# Revit family: PRD_FrankeWS_SnksSuprts_MaximaUnderframeToCommercialSinks_MAXF
name_source: partatom
category: Plumbing Fixtures
revit_build: Autodesk Revit 2018 (Build: 20190510_1515(x64)
units: mm (PartAtom-declared; Revit-internal decimal feet)

## family parameters
Always vertical = Yes
Cut with Voids When Loaded = No
OmniClass Number = 23.40.20.00
OmniClass Title = General Furniture and Specialties
Part Type = Normal
Room Calculation Point = No
Round Connector Dimension = Use Diameter
Shared = Yes
Work Plane-Based = No

## types (12) — shared parameters
AssetType = Fixed
Category = Pr_20_85_09_88, Sink supports
Color = stainless steel
DurationUnit = year
Features = stainless steel, 1.00 mm, satin finished, no mounting
Finish = satin finished
Form = Floor-standing
Height = 850 mm  [stored 2.78871 ft]
IfcExportAs = IfcBuildingElementProxy
IfcExportType = NOTDEFINED
Manufacturer = KWC Group AG
ManufacturerName = KWC Group AG
ManufacturerURL = www.kwc.com
Material = stainless steel
MaterialCode = stainless steel 1.4301
MaterialThickness = 1 mm  [stored 0.00328084 ft]
MaterialsBracketsBody = stainless steel
MaterialsBracketsFinishAndColour = satin finished
MaterialsLegsBody = stainless steel
MaterialsLegsFinishAndColour = satin finished
NBSDescription = Supports for sinks
NBSReference = 45-35-70/347
NominalHeight = 850 mm  [stored 2.78871 ft]
ProductInformation = https://pim.kwc.com
Shape = Rectangular
URL = www.kwc.com
UnderframeMaterial = PRD_AR_StainlessSteel_SatinFinished
Uniclass2015Code = Pr_20_85_09_88
Uniclass2015Title = Sink supports
Uniclass2015Version = Products v1.10
Version = 1
WarrantyDurationUnit = year

## per-type parameters (varying)
| type | BIMObjectName | Description | GrossWeight | Length | MAXF260 | MAXF60-200 | ModelNumber | Name | NetWeight | NominalLength | NominalWidth | Size | Width |
| MAXF60-60 | PRD_AR_SinkSupports_MaximaUnderframeToCommercialSinks_MAXF60-60 | Underframe to Maxima, stainless steel, 1.00 mm, satin finished,580x850x550 mm (WxHxD) | 32.00 kg | 580 mm  [stored 1.90289 ft] | No | Yes | 2000057122 | Underframe to Maxima sinks width 600 mm / depth 600 mm | 12.00 kg | 580 mm  [stored 1.90289 ft] | 550 mm | 580 x 550 x 850 mm | 550 mm |
| MAXF70-60 | PRD_AR_SinkSupports_MaximaUnderframeToCommercialSinks_MAXF70-60 | Underframe to Maxima, stainless steel, 1.00 mm, satin finished,680x850x550 mm (WxHxD) | 32.50 kg | 680 mm  [stored 2.23097 ft] | No | Yes | 2000057124 | Underframe to Maxima sinks width 700 mm / depth 600 mm | 12.50 kg | 680 mm  [stored 2.23097 ft] | 550 mm | 680 x 550 x 850 mm | 550 mm |
| MAXF70-70 | PRD_AR_SinkSupports_MaximaUnderframeToCommercialSinks_MAXF70-70 | Underframe to Maxima, stainless steel, 1.00 mm, satin finished,680x850x650 mm (WxHxD) | 33.50 kg | 680 mm  [stored 2.23097 ft] | No | Yes | 2000057126 | Underframe to Maxima sinks width 700 mm / depth 700 mm | 13.50 kg | 680 mm  [stored 2.23097 ft] | 650 mm  [stored 2.13255 ft] | 680 x 650 x 850 mm | 650 mm  [stored 2.13255 ft] |
| MAXF120-60 | PRD_AR_SinkSupports_MaximaUnderframeToCommercialSinks_MAXF120-60 | Underframe to Maxima, stainless steel, 1.00 mm, satin finished,1180x850x550 mm (WxHxD) | 35.00 kg | 1180 mm  [stored 3.87139 ft] | No | Yes | 2000057101 | Underframe to Maxima sinks width 1200 mm / depth 600 mm | 15.00 kg | 1180 mm  [stored 3.87139 ft] | 550 mm | 1180 x 550 x 850 mm | 550 mm |
| MAXF120-70 | PRD_AR_SinkSupports_MaximaUnderframeToCommercialSinks_MAXF120-70 | Underframe to Maxima, stainless steel, 1.00 mm, satin finished,1180x850x650 mm (WxHxD) | 36.00 kg | 1180 mm  [stored 3.87139 ft] | No | Yes | 2000057104 | Underframe to Maxima sinks width 1200 mm / depth 700 mm | 16.00 kg | 1180 mm  [stored 3.87139 ft] | 650 mm  [stored 2.13255 ft] | 1180 x 650 x 850 mm | 650 mm  [stored 2.13255 ft] |
| MAXF140-60 | PRD_AR_SinkSupports_MaximaUnderframeToCommercialSinks_MAXF140-60 | Underframe to Maxima, stainless steel, 1.00 mm, satin finished,1380x850x550 mm (WxHxD) | 33.50 kg | 1380 mm  [stored 4.52756 ft] | No | Yes | 2000057106 | Underframe to Maxima sinks width 1400 mm / depth 600 mm | 13.50 kg | 1380 mm  [stored 4.52756 ft] | 550 mm | 1380 x 550 x 850 mm | 550 mm |
| MAXF140-70 | PRD_AR_SinkSupports_MaximaUnderframeToCommercialSinks_MAXF140-70 | Underframe to Maxima, stainless steel, 1.00 mm, satin finished,1380x850x650 mm (WxHxD) | 36.50 kg | 1380 mm  [stored 4.52756 ft] | No | Yes | 2000057108 | Underframe to Maxima sinks width 1400 mm / depth 700 mm | 16.50 kg | 1380 mm  [stored 4.52756 ft] | 650 mm  [stored 2.13255 ft] | 1380 x 650 x 850 mm | 650 mm  [stored 2.13255 ft] |
| MAXF160-60 | PRD_AR_SinkSupports_MaximaUnderframeToCommercialSinks_MAXF160-60 | Underframe to Maxima, stainless steel, 1.00 mm, satin finished,1580x850x550 mm (WxHxD) | 34.50 kg | 1580 mm  [stored 5.18373 ft] | No | Yes | 2000057112 | Underframe to Maxima sinks width 1600 mm / depth 600 mm | 14.50 kg | 1580 mm  [stored 5.18373 ft] | 550 mm | 1580 x 550 x 850 mm | 550 mm |
| MAXF200-60 | PRD_AR_SinkSupports_MaximaUnderframeToCommercialSinks_MAXF200-60 | Underframe to Maxima, stainless steel, 1.00 mm, satin finished,1980x850x550 mm (WxHxD) | 36.50 kg | 1980 mm  [stored 6.49606 ft] | No | Yes | 2000057114 | Underframe to Maxima sinks width 2000 mm / depth 600 mm | 16.50 kg | 1980 mm  [stored 6.49606 ft] | 550 mm | 1980 x 550 x 850 mm | 550 mm |
| MAXF200-70 | PRD_AR_SinkSupports_MaximaUnderframeToCommercialSinks_MAXF200-70 | Underframe to Maxima, stainless steel, 1.00 mm, satin finished,1980x850x650 mm (WxHxD) | 39.00 kg | 1980 mm  [stored 6.49606 ft] | No | Yes | 2000057117 | Underframe to Maxima sinks width 2000 mm / depth 700 mm | 19.00 kg | 1980 mm  [stored 6.49606 ft] | 650 mm  [stored 2.13255 ft] | 1980 x 650 x 850 mm | 650 mm  [stored 2.13255 ft] |
| MAXF260-60 | PRD_AR_SinkSupports_MaximaUnderframeToCommercialSinks_MAXF260-60 | Underframe to Maxima, stainless steel, 1.00 mm, satin finished,2580x850x550 mm (WxHxD) | 40.50 kg | 2580 mm  [stored 8.46457 ft] | Yes | No | 2000057118 | Underframe to Maxima sinks width 2600 mm / depth 600 mm | 20.50 kg | 2580 mm  [stored 8.46457 ft] | 550 mm | 2580 x 550 x 850 mm | 550 mm |
| MAXF260-70 | PRD_AR_SinkSupports_MaximaUnderframeToCommercialSinks_MAXF260-70 | Underframe to Maxima, stainless steel, 1.00 mm, satin finished,2580x850x650 mm (WxHxD) | 42.50 kg | 2580 mm  [stored 8.46457 ft] | Yes | No | 2000057120 | Underframe to Maxima sinks width 2600 mm / depth 700 mm | 22.50 kg | 2580 mm  [stored 8.46457 ft] | 650 mm  [stored 2.13255 ft] | 2580 x 650 x 850 mm | 650 mm  [stored 2.13255 ft] |

note: column(s) folded — value = type name in every type: Model, ModelReference

note: [stored X ft] marks values corroborated as IEEE doubles in the binary element streams (Revit-internal decimal feet)

## geometry (parser evidence)
native form markers: Sweep x3
no freeform markers — native parametric forms only
